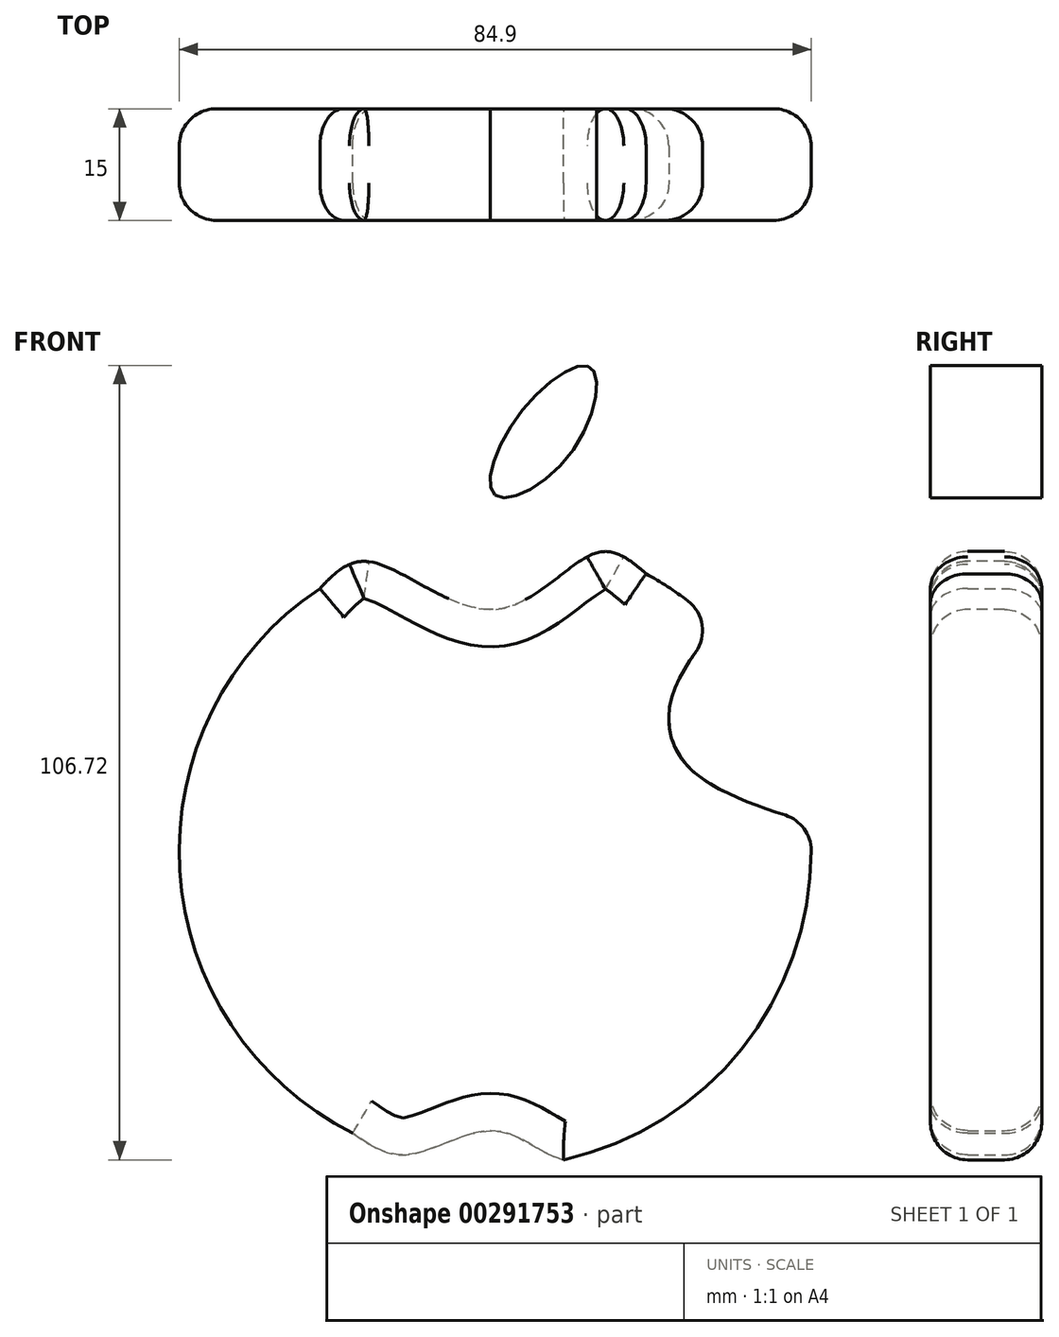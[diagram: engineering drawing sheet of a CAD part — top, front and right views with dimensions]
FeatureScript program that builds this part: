
annotation { "Feature Type Name" : "Feature", "Feature Type Description" : "" }
export const myFeature = defineFeature(function(context is Context, id is Id, definition is map)
    precondition{}
    {
        {
            var Q0;
            Q0=qCreatedBy(makeId("Front.planeOp"),FACE);
            var sketch = newSketch(context, id + "F0", { "sketchPlane" : qUnion([Q0])});
            skArc(sketch, "E0", {"start": v(9.16, -41.45) * mm, "mid": v(34.25, -25.07) * mm, "end": v(42.27, 3.8) * mm});
            skFitSpline(sketch, "E1", {"points": [v(-19.16, -37.87) * mm, v(-11.82, -40.77) * mm, v(0, -37.54) * mm, v(9.16, -41.45) * mm, v(16.05, -39.3) * mm], "startDerivative": vector(29.14, -20.45) * mm, "endDerivative": vector(30.62, 17.85) * mm});
            skFitSpline(sketch, "E2", {"points": [v(-23.55, 35.31) * mm, v(-16.94, 38.92) * mm, v(0, 32.5) * mm, v(13.77, 40.15) * mm, v(20.27, 37.3) * mm], "startDerivative": vector(28.05, 29.64) * mm, "endDerivative": vector(30.94, -26.77) * mm});
            skArc(sketch, "E3.trimOffspring", {"start": v(-23.55, 35.31) * mm, "mid": v(-42.37, -2.54) * mm, "end": v(-19.16, -37.87) * mm});
            skFitSpline(sketch, "E4", {"points": [v(0, 47.85) * mm, v(2.98, 58.38) * mm, v(12.82, 65.01) * mm, v(10.08, 53.34) * mm, v(0, 47.85) * mm]});
            skFitSpline(sketch, "E5", {"points": [v(29.67, 30.35) * mm, v(23.58, 20.15) * mm, v(25.87, 11.45) * mm, v(42.27, 3.8) * mm], "startDerivative": vector(-24.48, -31.11) * mm, "endDerivative": vector(49.4, -15.65) * mm});
            skArc(sketch, "E6.trimOffspring", {"start": v(29.67, 30.35) * mm, "mid": v(25.2, 34.15) * mm, "end": v(20.27, 37.3) * mm});
            skSolve(sketch);
        }
        {
            var Q0;
            Q0=makeQuery(id+"F0.imprint","IMPRINT",FACE,{"disambiguationData":[TD([[makeQuery(id+"F0.imprint","IMPRINT",EDGE,{"derivedFrom":sQuery(id+"F0.wireOp",EDGE,"E2")}),-1.0]])]});
            var Q1;
            Q1=makeQuery(id+"F0.imprint","IMPRINT",FACE,{"disambiguationData":[TD([[makeQuery(id+"F0.imprint","IMPRINT",EDGE,{"derivedFrom":sQuery(id+"F0.wireOp",EDGE,"E4")}),-1.0]])]});
            extrude(context, id + "F1", {"entities" : qUnion([Q0, Q1]), "depth" : 15 * mm});
        }
        {
            var Q0;
            Q0=makeQuery(id+"F1.opExtrude","SWEPT_EDGE",EDGE,{"disambiguationData":[OSD([sQuery(id+"F0.wireOp",EDGE,"E5"),sQuery(id+"F0.wireOp",EDGE,"E6.trimOffspring")])]});
            var Q1;
            Q1=makeQuery(id+"F1.opExtrude","SWEPT_EDGE",EDGE,{"disambiguationData":[OSD([sQuery(id+"F0.wireOp",EDGE,"E0"),sQuery(id+"F0.wireOp",EDGE,"E5")])]});
            fillet(context, id + "F2", {"entities" : qUnion([Q0, Q1]), "radius" : 5 * mm, "tangentPropagation" : true, "allowEdgeOverflow" : false});
        }
        {
            var Q0;
            Q0=makeQuery(id+"F1.opExtrude","CAP_FACE",FACE,{"disambiguationData":[OSD([sQuery(id+"F0.wireOp",EDGE,"E0"),sQuery(id+"F0.wireOp",EDGE,"E1"),sQuery(id+"F0.wireOp",EDGE,"E2"),sQuery(id+"F0.wireOp",EDGE,"E3.trimOffspring"),sQuery(id+"F0.wireOp",EDGE,"E5"),sQuery(id+"F0.wireOp",EDGE,"E6.trimOffspring")])],"isStart":false});
            var Q1;
            Q1=makeQuery(id+"F1.opExtrude","CAP_FACE",FACE,{"disambiguationData":[OSD([sQuery(id+"F0.wireOp",EDGE,"E0"),sQuery(id+"F0.wireOp",EDGE,"E1"),sQuery(id+"F0.wireOp",EDGE,"E2"),sQuery(id+"F0.wireOp",EDGE,"E3.trimOffspring"),sQuery(id+"F0.wireOp",EDGE,"E5"),sQuery(id+"F0.wireOp",EDGE,"E6.trimOffspring")])],"isStart":true});
            fillet(context, id + "F3", {"entities" : qUnion([Q0, Q1]), "radius" : 5 * mm, "tangentPropagation" : true, "allowEdgeOverflow" : false});
        }
    });
